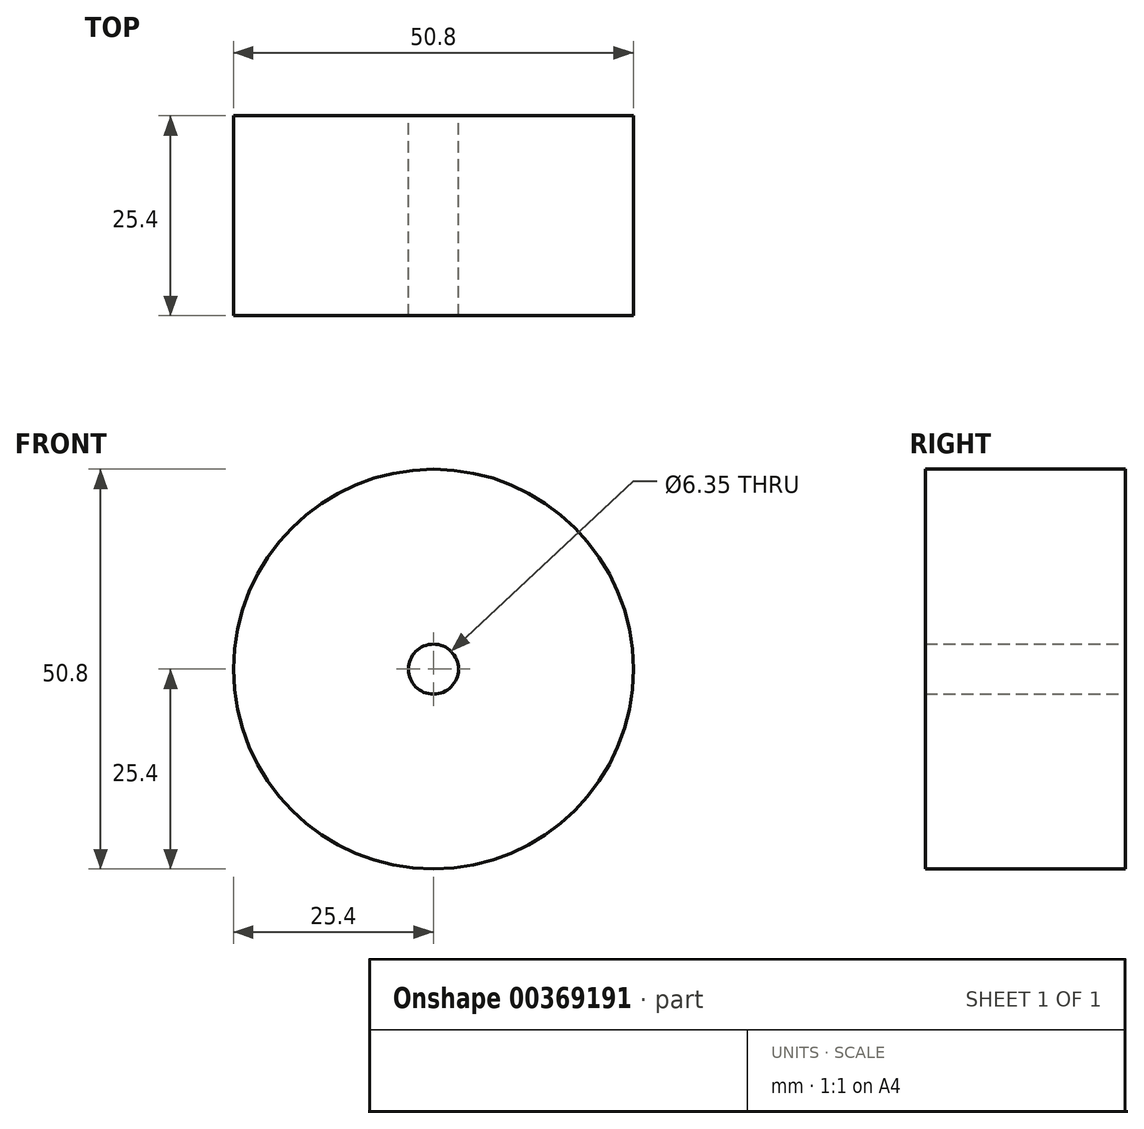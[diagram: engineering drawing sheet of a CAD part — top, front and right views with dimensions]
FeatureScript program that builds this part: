
annotation { "Feature Type Name" : "Feature", "Feature Type Description" : "" }
export const myFeature = defineFeature(function(context is Context, id is Id, definition is map)
    precondition{}
    {
        {
            var Q0;
            Q0=qCreatedBy(makeId("Front.planeOp"),FACE);
            var sketch = newSketch(context, id + "F0", { "sketchPlane" : qUnion([Q0])});
            skCircle(sketch, "E0", {"center": v(0, 0) * mm, "radius": 25.4 * mm});
            skCircle(sketch, "E1", {"center": v(0, 0) * mm, "radius": 3.18 * mm});
            skSolve(sketch);
        }
        {
            var Q0;
            Q0 = qSketchRegion(id + "F0", true);
            extrude(context, id + "F1", {"entities" : qUnion([Q0]), "depth" : 25.4 * mm, "symmetric" : true});
        }
    });
